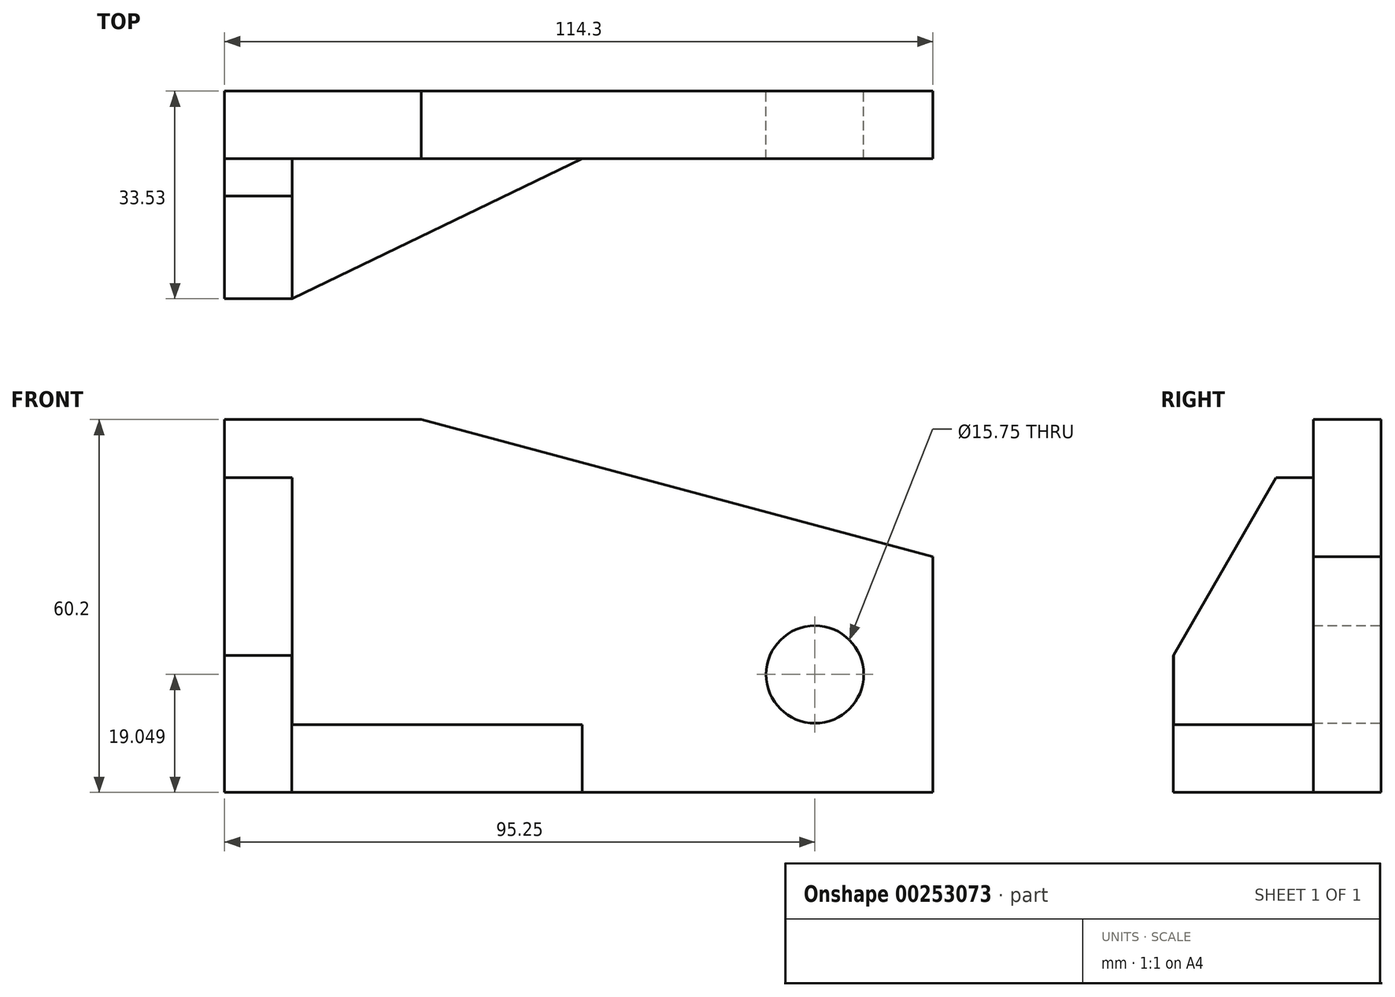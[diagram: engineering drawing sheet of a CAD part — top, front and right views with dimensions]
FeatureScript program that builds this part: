
annotation { "Feature Type Name" : "Feature", "Feature Type Description" : "" }
export const myFeature = defineFeature(function(context is Context, id is Id, definition is map)
    precondition{}
    {
        {
            var Q0;
            Q0=qCreatedBy(makeId("Front.planeOp"),FACE);
            var sketch = newSketch(context, id + "F0", { "sketchPlane" : qUnion([Q0])});
            skLineSegment(sketch, "E0.bottom", {"start": v(-57.38, 23.26) * mm, "end": v(56.92, 23.26) * mm});
            skLineSegment(sketch, "E0.top", {"start": v(-57.38, -36.94) * mm, "end": v(56.92, -36.94) * mm});
            skLineSegment(sketch, "E0.left", {"start": v(-57.38, 23.26) * mm, "end": v(-57.38, -36.94) * mm});
            skLineSegment(sketch, "E0.right", {"start": v(56.92, 23.26) * mm, "end": v(56.92, -36.94) * mm});
            skLineSegment(sketch, "E1", {"start": v(-57.38, 13.86) * mm, "end": v(-46.46, 13.86) * mm});
            skLineSegment(sketch, "E2", {"start": v(-46.46, 13.86) * mm, "end": v(-46.46, -36.94) * mm});
            skLineSegment(sketch, "E3", {"start": v(-46.46, -26.02) * mm, "end": v(6.12, -26.02) * mm});
            skLineSegment(sketch, "E4", {"start": v(6.12, -26.02) * mm, "end": v(6.12, -36.94) * mm});
            skCircle(sketch, "E5", {"center": v(37.87, -17.9) * mm, "radius": 7.87 * mm});
            skSolve(sketch);
        }
        {
            var Q0;
            {var subQ2=sQuery(id+"F0.wireOp",EDGE,"E0.bottom");Q0=makeQuery(id+"F0.imprint","IMPRINT",FACE,{"disambiguationData":[TD([[makeQuery(id+"F0.imprint","IMPRINT",EDGE,{"derivedFrom":subQ2}),-1.0]])]});}
            extrude(context, id + "F1", {"entities" : qUnion([Q0]), "depth" : 10.92 * mm});
        }
        {
            var Q0;
            {var subQ1=sQuery(id+"F0.wireOp",EDGE,"E1");Q0=makeQuery(id+"F0.imprint","IMPRINT",FACE,{"disambiguationData":[TD([[makeQuery(id+"F0.imprint","IMPRINT",EDGE,{"derivedFrom":subQ1}),-1.0]])]});}
            var Q1;
            {var subQ4=sQuery(id+"F0.wireOp",EDGE,"E3");Q1=makeQuery(id+"F0.imprint","IMPRINT",FACE,{"disambiguationData":[TD([[makeQuery(id+"F0.imprint","IMPRINT",EDGE,{"derivedFrom":subQ4}),-1.0]])]});}
            extrude(context, id + "F2", {"entities" : qUnion([Q0, Q1]), "operationType" : NewBodyOperationType.ADD, "depth" : 33.53 * mm});
        }
        {
            var Q0;
            Q0=makeQuery(id+"F1.opExtrude","SWEPT_EDGE",EDGE,{"disambiguationData":[OSD([sQuery(id+"F0.wireOp",EDGE,"E0.bottom"),sQuery(id+"F0.wireOp",EDGE,"E0.right")])]});
            chamfer(context, id + "F3", {"entities" : qUnion([Q0]), "chamferType" : ChamferType.OFFSET_ANGLE, "width" : 82.55 * mm, "oppositeDirection" : false, "angle" : 15 * degree, "tangentPropagation" : true});
        }
        {
            var Q0;
            Q0=makeQuery(id+"F2.opExtrude","CAP_EDGE",EDGE,{"disambiguationData":[OSD([sQuery(id+"F0.wireOp",EDGE,"E4")])],"isStart":false});
            chamfer(context, id + "F4", {"entities" : qUnion([Q0]), "chamferType" : ChamferType.OFFSET_ANGLE, "width" : 25.4 * mm, "oppositeDirection" : false, "angle" : 64.25 * degree, "tangentPropagation" : true});
        }
        {
            var Q0;
            Q0=makeQuery(id+"F2.opExtrude","CAP_EDGE",EDGE,{"disambiguationData":[OSD([sQuery(id+"F0.wireOp",EDGE,"E1")])],"isStart":false});
            chamfer(context, id + "F5", {"entities" : qUnion([Q0]), "chamferType" : ChamferType.OFFSET_ANGLE, "width" : 28.7 * mm, "oppositeDirection" : true, "angle" : 30 * degree, "tangentPropagation" : true});
        }
    });
